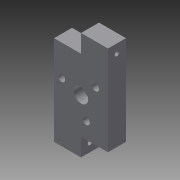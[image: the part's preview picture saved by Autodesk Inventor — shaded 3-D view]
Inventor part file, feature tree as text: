
AUTODESK INVENTOR PART (.ipt)
format: ipt  version: 2013 (Build 170138000, 138)  size: 111,616 bytes
history: native  units: in
note: dims shown in document units (in); Inventor stores cm internally (conversion verified against a paired STEP export)
features: extrude x6, sketch x6, reference x1
ambient origin geometry x8: Origin, YZ Plane, XZ Plane, XY Plane, X Axis, Y Axis, Z Axis, Center Point
bodies: Solid1 (feature_tree)
feature tree (13):
  extrude  "Extrusion1"  Depth=3.0in
  extrude  "Extrusion2"  Depth=0.75in
  extrude  "Extrusion3"  Depth=0.5in TaperAngle=0.0deg
  extrude  "Extrusion4"  Depth=0.5in
  extrude  "Extrusion5"  Depth=0.4in
  extrude  "Extrusion9"  Depth=0.125in
  sketch  "Sketch1"  dims[d0=1.5in d1=3.0in]
  sketch  "Sketch2"  dims[d2=0.5in d3=0.0in d4=0.75in]
  sketch  "Sketch3"  dims[d5=0.5in d6=0.5in d7=0.0in]
  sketch  "Sketch4"  dims[d8=0.75in d9=0.5in]
  sketch  "Sketch5"  dims[d10=0.5in d11=0.0in d12=0.4in]
  sketch  "Sketch9"  dims[d13=0.25in d14=0.0in d16=0.125in d17=0.25in d18=0.25in d19=0.25in d20=0.25in d21=0.75in d22=0.0in d34=0.125in d35=0.25in d36=0.1925in d37=0.1925in d38=0.75in d39=0.0in]
  reference  "Reference4"
